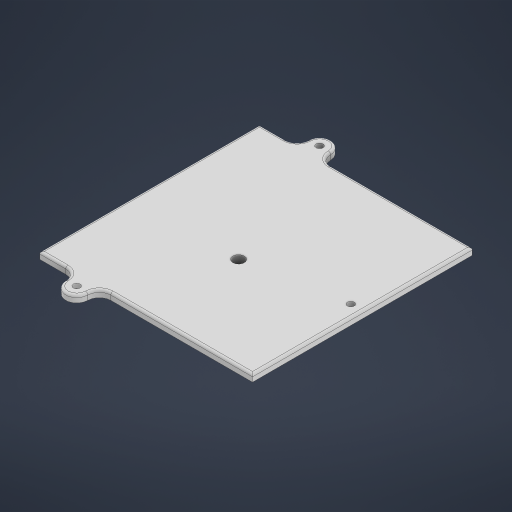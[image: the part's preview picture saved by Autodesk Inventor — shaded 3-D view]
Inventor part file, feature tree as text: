
AUTODESK INVENTOR PART (.ipt)
format: ipt  version: 2024.2 (Build 282272000, 272)  size: 857,088 bytes
history: native  units: in
note: dims shown in document units (in); Inventor stores cm internally (conversion verified against a paired STEP export)
features: sketch x4, extrude x4, fillet x1, chamfer x1
ambient origin geometry x8: Origin, YZ Plane, XZ Plane, XY Plane, X Axis, Y Axis, Z Axis, Center Point
bodies: Solid1 (feature_tree)
feature tree (10):
  sketch  "Sketch1"  dims[d2=3.7402in d10=0.1181in d11=0.0in d12=0.0394in]
  extrude  "Extrusion1"  Depth=0.1181in TaperAngle=0.0deg
  fillet  "Fillet1"  Radius=0.0394in
  extrude  "Extrusion3"  Depth=0.0787in
  sketch  "Sketch2"  dims[d13=0.0787in d14=0.0787in]
  chamfer  "Chamfer2"  Distance=0.0787in
  extrude  "Extrusion4"  TaperAngle=135.0deg  [1 undecoded]
  extrude  "Extrusion5"  Depth=0.0787in
  sketch  "Sketch3"  dims[d15=0.0787in]
  sketch  "Sketch4"  dims[d16=0.0787in d17=0.0787in d18=135.0deg d20=0.0787in d21=0.0787in d22=0.0787in d23=0.0787in d24=0.0787in d25=0.0787in d26=0.0787in d28=135.0deg d29=0.0787in d30=0.0787in d31=0.0787in d32=0.0787in d33=45.0deg d35=0.0787in d36=0.0787in d39=0.0787in d40=0.0787in d41=0.0787in d42=0.0787in d43=0.0787in d44=0.0394in d45=0.1575in d50=0.1181in d51=0.0787in d52=0.0787in d53=0.0787in d54=0.0787in d55=0.0in d61=0.1378in d62=0.1378in d63=0.1378in d64=0.1378in d65=0.1378in d66=135.0deg d67=0.1378in d68=0.1378in d69=0.1378in d70=0.1378in d71=0.1378in d72=0.1378in d73=0.1378in d74=135.0deg d75=0.1378in d76=0.1378in d77=0.1378in d78=0.1378in d79=45.0deg d80=0.1378in d81=0.1378in d82=0.1378in d83=0.1378in d84=0.1378in d85=0.1378in d86=0.1378in d87=0.0689in d88=0.2756in d89=0.2067in d90=0.1378in d91=0.1378in d92=0.1378in d93=0.1378in d94=0.0in d96=0.0787in d97=0.0in d98=0.0591in d99=0.0787in d100=45.0deg d101=0.8268in d102=0.1181in d103=0.374in d104=0.1969in d105=0.1969in d106=0.1969in d107=0.1181in d108=0.1969in d109=3.622in d110=0.2756in d111=0.2756in d112=0.0394in d113=0.0in d114=0.1969in d115=0.0394in d116=0.0in]
note: 1 required parameter value undecoded (feature->parameter linkage not recoverable at this tier; creation-order binding heuristic only, values carry confidence <= 0.55)
